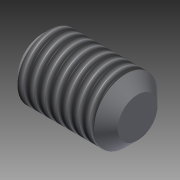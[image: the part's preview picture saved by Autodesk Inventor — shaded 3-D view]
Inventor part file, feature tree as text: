
AUTODESK INVENTOR PART (.ipt)
format: ipt  version: 2014 SP2 (Build 180246200, 246)  size: 131,584 bytes
history: native  units: mm
features: other x7, sketch x3, revolve x2, thread x1, extrude x1
ambient origin geometry x8: Origin, YZ Plane, XZ Plane, XY Plane, X Axis, Y Axis, Z Axis, Center Point
bodies: Solid1 (feature_tree)
feature tree (14):
  revolve  "Revolution1"  [1 undecoded]
  thread  "Thread1"  [1 undecoded]
  extrude  "Extrusion1"  TaperAngle=0.0deg  [1 undecoded]
  revolve  "Revolution2"  [1 undecoded]
  other  "CP_XY"
  other  "CP_YZ"
  other  "CP_ZX"
  other  "CP_X"
  other  "CP_Y"
  other  "CP_Z"
  other  "CP_Center"
  sketch  "Sketch_1"  dims[d0=360.0deg d1=4.8205mm d2=0.0mm d3=1.5mm d4=0.0mm]
  sketch  "Sketch_2"  dims[d5=360.0deg d6=0.0mm]
  sketch  "Sketch_3"
note: 4 required parameter values undecoded (feature->parameter linkage not recoverable at this tier; creation-order binding heuristic only, values carry confidence <= 0.55)